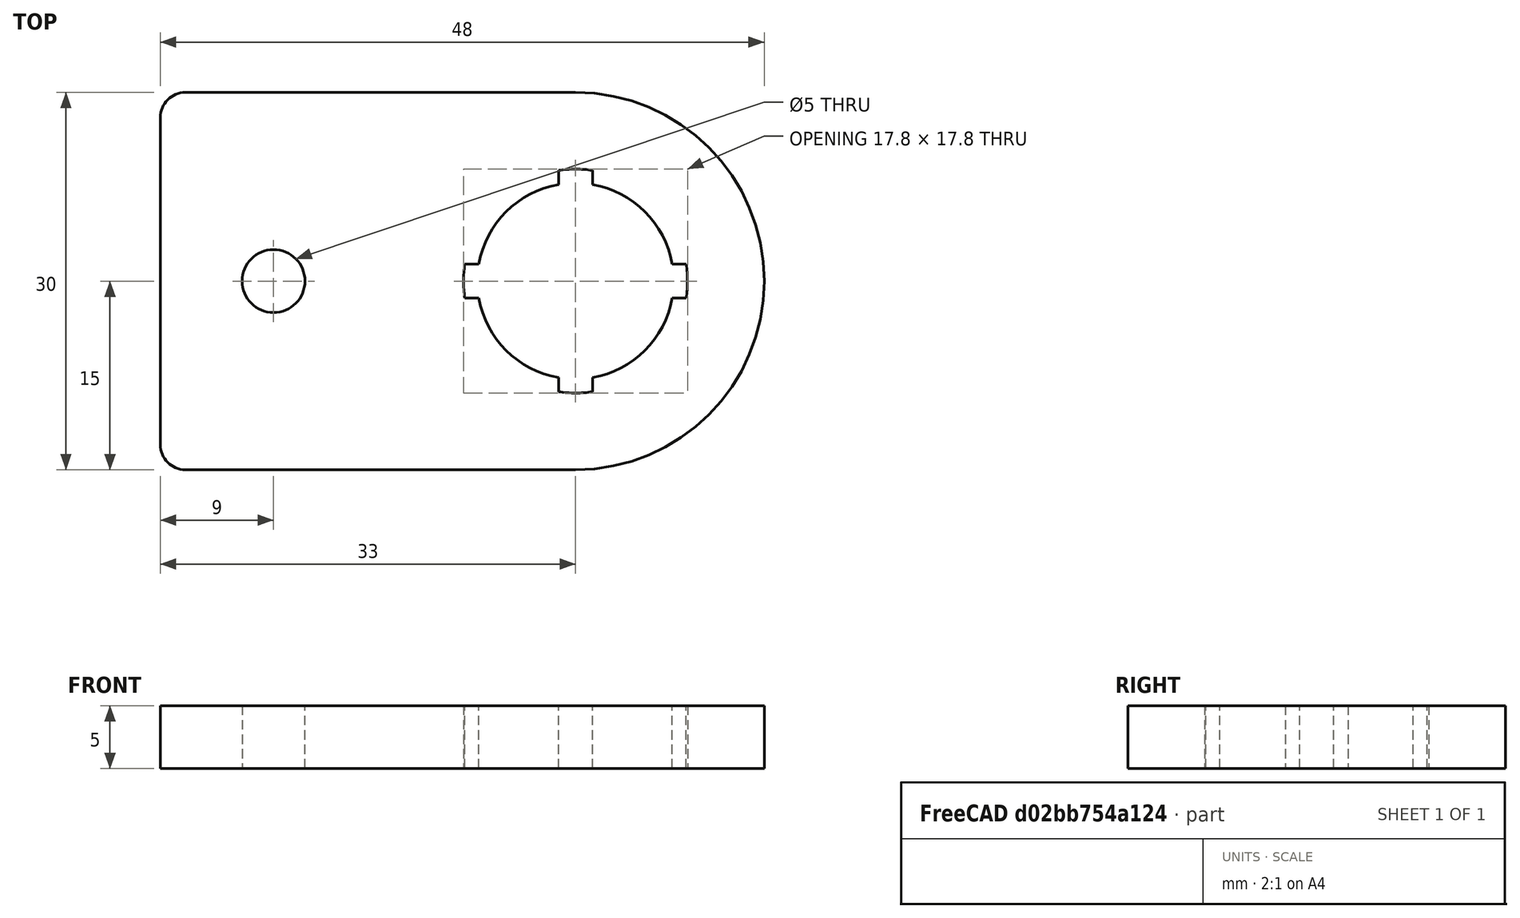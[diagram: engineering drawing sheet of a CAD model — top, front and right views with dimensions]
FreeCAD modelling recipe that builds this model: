
FCSTD DOCUMENT  (FreeCAD 0.19R24366 (Git))
Label: Actuator extension socket bracket
License: All rights reserved
LicenseURL: http://en.wikipedia.org/wiki/All_rights_reserved
objects: Sketcher::SketchObject×1, PartDesign::Pad×1, PartDesign::Body×1
note: 4 computed .brp shape members not serialized (recipe doc carries the construction recipe); baked Part::Feature solids carry a one-line shape summary decoded from their .brp

FEATURE [Sketcher::SketchObject] Sketch
  FullyConstrained = true
  MapMode = 5
  Support = -> [XY_Plane]
  sketch-geometry (26):
    g0: LineSegment StartX=-7 StartY=15 StartZ=0 EndX=24 EndY=15 EndZ=0
    g1: LineSegment StartX=-7 StartY=-15 StartZ=0 EndX=24 EndY=-15 EndZ=0
    g2: LineSegment StartX=-9 StartY=13 StartZ=0 EndX=-9 EndY=-13 EndZ=0
    g3: ArcOfCircle CenterX=-7 CenterY=13 CenterZ=0 NormalX=0 NormalY=0 NormalZ=1 AngleXU=0 Radius=2 StartAngle=1.5708 EndAngle=3.14159
    g4: ArcOfCircle CenterX=-7 CenterY=-13 CenterZ=0 NormalX=0 NormalY=0 NormalZ=1 AngleXU=0 Radius=2 StartAngle=3.14159 EndAngle=4.71239
    g5: ArcOfCircle CenterX=24 CenterY=-8e-16 CenterZ=0 NormalX=0 NormalY=0 NormalZ=1 AngleXU=0 Radius=15 StartAngle=4.71239 EndAngle=7.85398
    g6: ArcOfCircle CenterX=24 CenterY=-8e-16 CenterZ=0 NormalX=0 NormalY=0 NormalZ=1 AngleXU=0 Radius=7.8 StartAngle=3.31555 EndAngle=4.53844
    g7: Circle CenterX=0 CenterY=0 CenterZ=0 NormalX=0 NormalY=0 NormalZ=1 AngleXU=0 Radius=2.5
    g8: LineSegment StartX=10 StartY=15 StartZ=0 EndX=10 EndY=-15 EndZ=0
    g9: Circle CenterX=24 CenterY=-8e-16 CenterZ=0 NormalX=0 NormalY=0 NormalZ=1 AngleXU=0 Radius=11
    g10: ArcOfCircle CenterX=24 CenterY=-8e-16 CenterZ=0 NormalX=0 NormalY=0 NormalZ=1 AngleXU=0 Radius=8.9 StartAngle=2.98932 EndAngle=3.29387
    g11: LineSegment StartX=15.203 StartY=1.35 StartZ=0 EndX=16.3177 EndY=1.35 EndZ=0
    g12: LineSegment StartX=15.203 StartY=-1.35 StartZ=0 EndX=16.3177 EndY=-1.35 EndZ=0
    g13: LineSegment StartX=31.6823 StartY=1.35 StartZ=0 EndX=32.797 EndY=1.35 EndZ=0
    g14: LineSegment StartX=31.6823 StartY=-1.35 StartZ=0 EndX=32.797 EndY=-1.35 EndZ=0
    g15: LineSegment StartX=22.65 StartY=8.79702 StartZ=0 EndX=22.65 EndY=7.68228 EndZ=0
    g16: LineSegment StartX=25.35 StartY=8.79702 StartZ=0 EndX=25.35 EndY=7.68228 EndZ=0
    g17: LineSegment StartX=22.65 StartY=-7.68228 StartZ=0 EndX=22.65 EndY=-8.79702 EndZ=0
    g18: LineSegment StartX=25.35 StartY=-7.68228 StartZ=0 EndX=25.35 EndY=-8.79702 EndZ=0
    g19: LineSegment StartX=24 StartY=15 StartZ=0 EndX=24 EndY=-15 EndZ=0
    g20: ArcOfCircle CenterX=24 CenterY=-8e-16 CenterZ=0 NormalX=0 NormalY=0 NormalZ=1 AngleXU=0 Radius=8.9 StartAngle=1.41852 EndAngle=1.72307
    g21: ArcOfCircle CenterX=24 CenterY=-8e-16 CenterZ=0 NormalX=0 NormalY=0 NormalZ=1 AngleXU=0 Radius=8.9 StartAngle=6.13091 EndAngle=6.43546
    g22: ArcOfCircle CenterX=24 CenterY=-8e-16 CenterZ=0 NormalX=0 NormalY=0 NormalZ=1 AngleXU=0 Radius=8.9 StartAngle=4.56012 EndAngle=4.86466
    g23: ArcOfCircle CenterX=24 CenterY=-8e-16 CenterZ=0 NormalX=0 NormalY=0 NormalZ=1 AngleXU=0 Radius=7.8 StartAngle=1.74475 EndAngle=2.96764
    g24: ArcOfCircle CenterX=24 CenterY=-8e-16 CenterZ=0 NormalX=0 NormalY=0 NormalZ=1 AngleXU=0 Radius=7.8 StartAngle=0.173953 EndAngle=1.39684
    g25: ArcOfCircle CenterX=24 CenterY=-8e-16 CenterZ=0 NormalX=0 NormalY=0 NormalZ=1 AngleXU=0 Radius=7.8 StartAngle=4.88634 EndAngle=6.10923
  constraints (75):
    c: Horizontal(g0)
    c: Horizontal(g1)
    c: Tangent(g0,g3) = 1.5708
    c: Tangent(g2,g3) = -1.5708
    c: Tangent(g2,g4) = -1.5708
    c: Tangent(g1,g4) = -1.5708
    c: Symmetric(g2,g2,g-1)
    c: Equal(g3,g4)
    c: Radius(g3) = 2
    c: DistanceY(g1,g0) = 30
    c: DistanceX(g2,g-1) = 9
    c: Tangent(g5,g1) = -1.5708
    c: Coincident(g5,g0)
    c: Coincident(g6,g5)
    c: Diameter(g6) = 15.6
    c: DistanceX(g-1,g5) = 24
    c: Coincident(g7,g-1)
    c: PointOnObject(g8,g0)
    c: PointOnObject(g8,g1)
    c: Vertical(g8)
    c: DistanceX(g7,g8) = 10
    c: Coincident(g9,g5)
    c: Diameter(g9) = 22
    c: Diameter(g7) = 5
    c: Coincident(g10,g5)
    c: Diameter(g10) = 17.8
    c: Horizontal(g11)
    c: Horizontal(g12)
    c: Horizontal(g13)
    c: Horizontal(g14)
    c: PointOnObject(g15,g6)
    c: Vertical(g15)
    c: Vertical(g17)
    c: PointOnObject(g18,g6)
    c: Coincident(g19,g1)
    c: Vertical(g19)
    c: Coincident(g0,g19)
    c: Coincident(g10,g11)
    c: Coincident(g20,g15)
    c: Equal(g10,g20)
    c: Coincident(g21,g13)
    c: Coincident(g20,g16)
    c: Coincident(g10,g20)
    c: Equal(g10,g21)
    c: Coincident(g22,g18)
    c: Coincident(g21,g14)
    c: Coincident(g10,g21)
    c: Equal(g10,g22)
    c: Coincident(g10,g12)
    c: Coincident(g22,g17)
    c: Coincident(g10,g22)
    c: Coincident(g6,g12)
    c: Coincident(g23,g11)
    c: Equal(g6,g23)
    c: Coincident(g24,g16)
    c: Coincident(g6,g23)
    c: Equal(g6,g24)
    c: Coincident(g25,g14)
    c: Coincident(g24,g13)
    c: Coincident(g6,g24)
    c: PointOnObject(g23,g15)
    c: Equal(g6,g25)
    c: Coincident(g6,g17)
    c: Coincident(g6,g25)
    c: PointOnObject(g25,g18)
    c: Vertical(g18)
    c: Equal(g11,g12)
    c: Equal(g12,g17)
    c: Equal(g17,g18)
    c: Equal(g18,g14)
    c: Equal(g14,g13)
    c: Equal(g13,g16)
    c: Equal(g16,g15)
    c: Vertical(g16)
    c: DistanceY(g14,g13) = 2.7
FEATURE [PartDesign::Pad] Pad
  Direction = (1,1,1)
  Length = 5
  Length2 = 100
  Profile = -> Sketch
  Type = 0
FEATURE [PartDesign::Body] Body
  Group = -> [Sketch,Pad]
  Origin = -> Origin
  Tip = -> Pad
